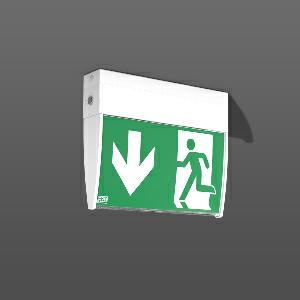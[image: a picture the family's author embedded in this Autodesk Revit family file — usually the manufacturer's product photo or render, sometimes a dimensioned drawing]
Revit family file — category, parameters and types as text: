
# Revit family: gsun_d_652219_002_ca78
name_source: partatom
category: Lighting Fixtures
units: mm (PartAtom-declared; Revit-internal decimal feet)

## family parameters
Cut with Voids When Loaded = No
Host = Face
Light Source = No
Part Type = Normal
Room Calculation Point = No
Round Connector Dimension = Use Diameter
Shared = No

## types (1)
- GSUN D
    Apparent Load = 0 VA
    Approval mark = CE
    Default Elevation = 1800 mm
    Description = Series: GSUN D
Luminaire for escape route identification. Housing: extruded aluminium profile, powder-coated. 4 legends and 1 white lay in plastic sheet included. Universal mounting kit for ceiling and wall surface mounting. Electronic ballast included. Self-contained system with automatic self-test. With NFC programming interface. 
Colour: white
Length: 247 mm
Width: 45 mm
Height: 200 mm
Weight: 0.9 kg
Operating mode: maintained power mode
Viewing Distance: 24 m
Duration time: 1 h, 3 h, 8 h
Lamp: LED
Socket: without socket
Colour temperature: 4000K
System power: 2 W
Control gear: Regulated power supply
Protection class: I
Type of protection: IP 30
    Height = 200 mm  [stored 0.656168 ft]
    Lamp = 0 x
    Length = 247 mm
    Luminous efficacy = 0 lm/W
    Manufacturer = RZB
    ModVariant = No
    Model = 652219.002
    Mounting Place = Ceiling, Wall
    Mounting Type = Surface mounted
    Number of Poles = 1
    OnlyDefault = Yes
    Power Factor = 1
    Product Name = GSUN D
    Product group = Surface mounted ceiling and wall luminaires
    ProductGroupID = 305
    Protection Class = Protection class I
    Protection Degree = IP 30
    RLX_Detail_Level = 1
    RLX_Emergency_Light_Flux = 0 lm
    RLX_Emergency_Type = 0
    RLX_Emergency_Type_DB = No
    RlxData = <blob elided: 29973 chars, md5=db926892>
    Standby Power = 0 W
    System Light Flux = 0 lm
    System Power = 0 W
    Type Comments = Product without accessories
    Type Image = 671995.002.1.jpg
    URL = http://relux.com
    VarID = ---
    Voltage = 230 V
    Voltage Range = 220-240 V
    Weight = 0.00 kg
    Width = 45 mm

note: [stored X ft] marks values corroborated as IEEE doubles in the binary element streams (Revit-internal decimal feet)

## geometry (parser evidence)
native form markers: Blend x4, Sweep x9
no freeform markers — native parametric forms only
